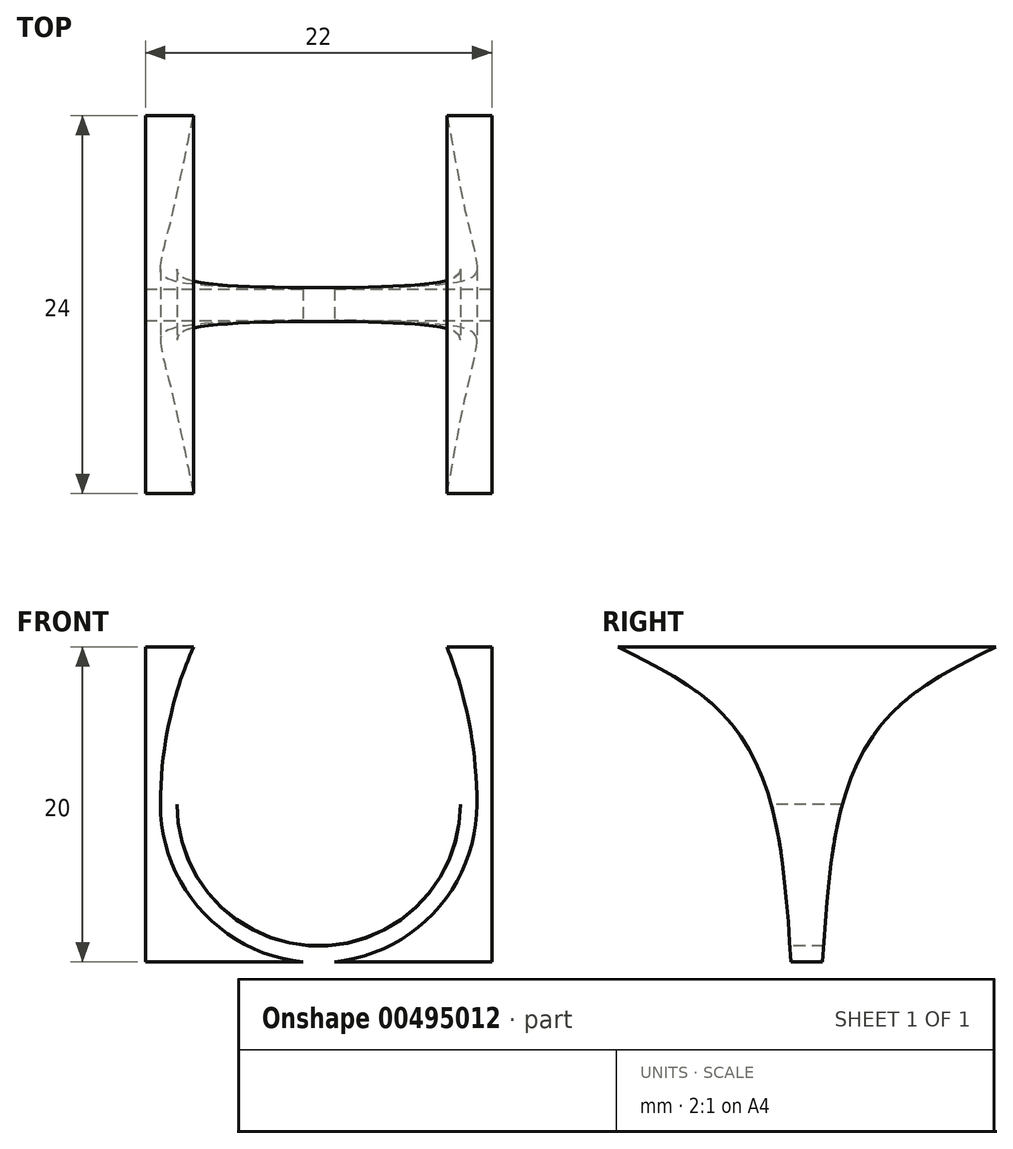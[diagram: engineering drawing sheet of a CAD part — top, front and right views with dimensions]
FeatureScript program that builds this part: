
annotation { "Feature Type Name" : "Feature", "Feature Type Description" : "" }
export const myFeature = defineFeature(function(context is Context, id is Id, definition is map)
    precondition{}
    {
        {
            var Q0;
            Q0=qCreatedBy(makeId("Front.planeOp"),FACE);
            var sketch = newSketch(context, id + "F0", { "sketchPlane" : qUnion([Q0])});
            skLineSegment(sketch, "E0", {"start": v(11, 0) * mm, "end": v(-11, 0) * mm});
            skLineSegment(sketch, "E1.top", {"start": v(11, -20) * mm, "end": v(-11, -20) * mm});
            skLineSegment(sketch, "E1.left", {"start": v(11, 0) * mm, "end": v(11, -20) * mm});
            skLineSegment(sketch, "E1.right", {"start": v(-11, 0) * mm, "end": v(-11, -20) * mm});
            skSolve(sketch);
        }
        {
            var Q0;
            Q0=makeQuery(id+"F0.imprint","IMPRINT",FACE,{"disambiguationData":[TD([[makeQuery(id+"F0.imprint","IMPRINT",EDGE,{"derivedFrom":sQuery(id+"F0.wireOp",EDGE,"E0")}),1.0]])]});
            extrude(context, id + "F1", {"entities" : qUnion([Q0]), "endBound" : BoundingType.SYMMETRIC, "depth" : 24 * mm});
        }
        {
            var Q0;
            Q0=makeQuery(id+"F1.opExtrude","SWEPT_FACE",FACE,{"disambiguationData":[OSD([sQuery(id+"F0.wireOp",EDGE,"E1.left")])]});
            var sketch = newSketch(context, id + "F2", { "sketchPlane" : qUnion([Q0])});
            skLineSegment(sketch, "E2", {"start": v(0, 0) * mm, "end": v(0, -20) * mm});
            skLineSegment(sketch, "E3", {"start": v(0, -20) * mm, "end": v(1, -20) * mm});
            skFitSpline(sketch, "E4", {"points": [v(1, -20) * mm, v(2.4, -9.52) * mm, v(5.93, -3.69) * mm, v(12, 0) * mm], "startDerivative": vector(1.93, 29.44) * mm, "endDerivative": vector(21.05, 10.36) * mm});
            skLineSegment(sketch, "E5", {"start": v(12, 0) * mm, "end": v(0, 0) * mm});
            skFitSpline(sketch, "E6.MirrorCS", {"points": [v(-1, -20) * mm, v(-2.4, -9.52) * mm, v(-5.93, -3.69) * mm, v(-12, 0) * mm], "startDerivative": vector(-1.93, 29.44) * mm, "endDerivative": vector(-21.05, 10.36) * mm});
            skLineSegment(sketch, "E7.MirrorCS", {"start": v(-12, 0) * mm, "end": v(0, 0) * mm});
            skSolve(sketch);
        }
        {
            var Q0;
            {var subQ0=sQuery(id+"F2.wireOp",EDGE,"E6.MirrorCS");Q0=makeQuery(id+"F2.imprint","IMPRINT",FACE,{"disambiguationData":[TD([[makeQuery(id+"F2.imprint","IMPRINT",EDGE,{"derivedFrom":subQ0}),1.0]])]});}
            var Q1;
            {var subQ0=sQuery(id+"F2.wireOp",EDGE,"E4");Q1=makeQuery(id+"F2.imprint","IMPRINT",FACE,{"disambiguationData":[TD([[makeQuery(id+"F2.imprint","IMPRINT",EDGE,{"derivedFrom":subQ0}),-1.0]])]});}
            extrude(context, id + "F3", {"entities" : qUnion([Q0, Q1]), "operationType" : NewBodyOperationType.REMOVE, "oppositeDirection" : true, "depth" : 25.4 * mm});
        }
        {
            var Q0;
            Q0=qCreatedBy(makeId("Front.planeOp"),FACE);
            var sketch = newSketch(context, id + "F4", { "sketchPlane" : qUnion([Q0])});
            skCircle(sketch, "E8", {"center": v(0, -10) * mm, "radius": 9 * mm});
            skArc(sketch, "E9", {"start": v(0.09, 0.05) * mm, "mid": v(0, 0.05) * mm, "end": v(-0.09, 0.05) * mm});
            skLineSegment(sketch, "E10", {"start": v(0, 0.05) * mm, "end": v(11.24, 0) * mm});
            skLineSegment(sketch, "E11", {"start": v(11.24, 0) * mm, "end": v(11.24, -20.05) * mm});
            skLineSegment(sketch, "E12", {"start": v(11.24, -20.05) * mm, "end": v(0, -20.05) * mm});
            skLineSegment(sketch, "E13.MirrorCS", {"start": v(0, 0.05) * mm, "end": v(-11.24, 0) * mm});
            skLineSegment(sketch, "E14.MirrorCS", {"start": v(-11.24, 0) * mm, "end": v(-11.24, -20.05) * mm});
            skLineSegment(sketch, "E15.MirrorCS", {"start": v(-11.24, -20.05) * mm, "end": v(0, -20.05) * mm});
            skPoint(sketch, "E16.start.orphan", {"position": v(0, 0) * mm});
            skPoint(sketch, "E17.end.orphan", {"position": v(0, -20) * mm});
            skPoint(sketch, "E17.start.orphan", {"position": v(0, -19) * mm});
            skArc(sketch, "E18.trimOffspring", {"start": v(-10.05, -10) * mm, "mid": v(0, -20.05) * mm, "end": v(10.05, -10) * mm});
            skArc(sketch, "E19", {"start": v(-7.95, 0.01) * mm, "mid": v(-9.52, -4.88) * mm, "end": v(-10.05, -10) * mm});
            skLineSegment(sketch, "E20", {"start": v(-10.05, 0) * mm, "end": v(-7.95, 0.01) * mm});
            skArc(sketch, "E21", {"start": v(10.05, -10) * mm, "mid": v(9.57, -4.9) * mm, "end": v(8.14, 0.01) * mm});
            skSolve(sketch);
        }
        {
            var Q0;
            {var subQ0=sQuery(id+"F4.wireOp",EDGE,"E10");Q0=makeQuery(id+"F4.imprint","IMPRINT",FACE,{"disambiguationData":[TD([[makeQuery(id+"F4.imprint","IMPRINT",EDGE,{"derivedFrom":subQ0}),-1.0]])]});}
            var Q1;
            {var subQ0=sQuery(id+"F4.wireOp",EDGE,"E13.MirrorCS");Q1=makeQuery(id+"F4.imprint","IMPRINT",FACE,{"disambiguationData":[TD([[makeQuery(id+"F4.imprint","IMPRINT",EDGE,{"derivedFrom":subQ0}),1.0]])]});}
            extrude(context, id + "F5", {"entities" : qUnion([Q0, Q1]), "operationType" : NewBodyOperationType.REMOVE, "endBound" : BoundingType.SYMMETRIC, "oppositeDirection" : true, "depth" : 25.4 * mm});
        }
        {
            var Q0;
            Q0=qCreatedBy(makeId("Front.planeOp"),FACE);
            var sketch = newSketch(context, id + "F6", { "sketchPlane" : qUnion([Q0])});
            skCircle(sketch, "E22", {"center": v(0, -9.98) * mm, "radius": 9 * mm});
            skPoint(sketch, "E23.start.orphan", {"position": v(0, -19.96) * mm});
            skSolve(sketch);
        }
        {
            var Q0;
            Q0 = qSketchRegion(id + "F6", true);
            extrude(context, id + "F7", {"entities" : qUnion([Q0]), "operationType" : NewBodyOperationType.REMOVE, "endBound" : BoundingType.SYMMETRIC, "oppositeDirection" : true, "depth" : 25.4 * mm});
        }
        {
            var Q0;
            Q0=makeQuery(id+"F1.opExtrude","SWEPT_FACE",FACE,{"disambiguationData":[OSD([sQuery(id+"F0.wireOp",EDGE,"E0")])]});
            var sketch = newSketch(context, id + "F8", { "sketchPlane" : qUnion([Q0])});
            skCircle(sketch, "E24", {"center": v(0, 0) * mm, "radius": 2.5 * mm});
            skSolve(sketch);
        }
        {
            var Q0;
            Q0=makeQuery(id+"F8.imprint","IMPRINT",FACE,{"disambiguationData":[TD([[makeQuery(id+"F8.imprint","IMPRINT",EDGE,{"derivedFrom":sQuery(id+"F8.wireOp",EDGE,"E24")}),1.0]])]});
            extrude(context, id + "F9", {"entities" : qUnion([Q0]), "operationType" : NewBodyOperationType.REMOVE, "oppositeDirection" : true, "depth" : 5 * mm, "offsetDistance" : 25.4 * mm});
        }
    });
